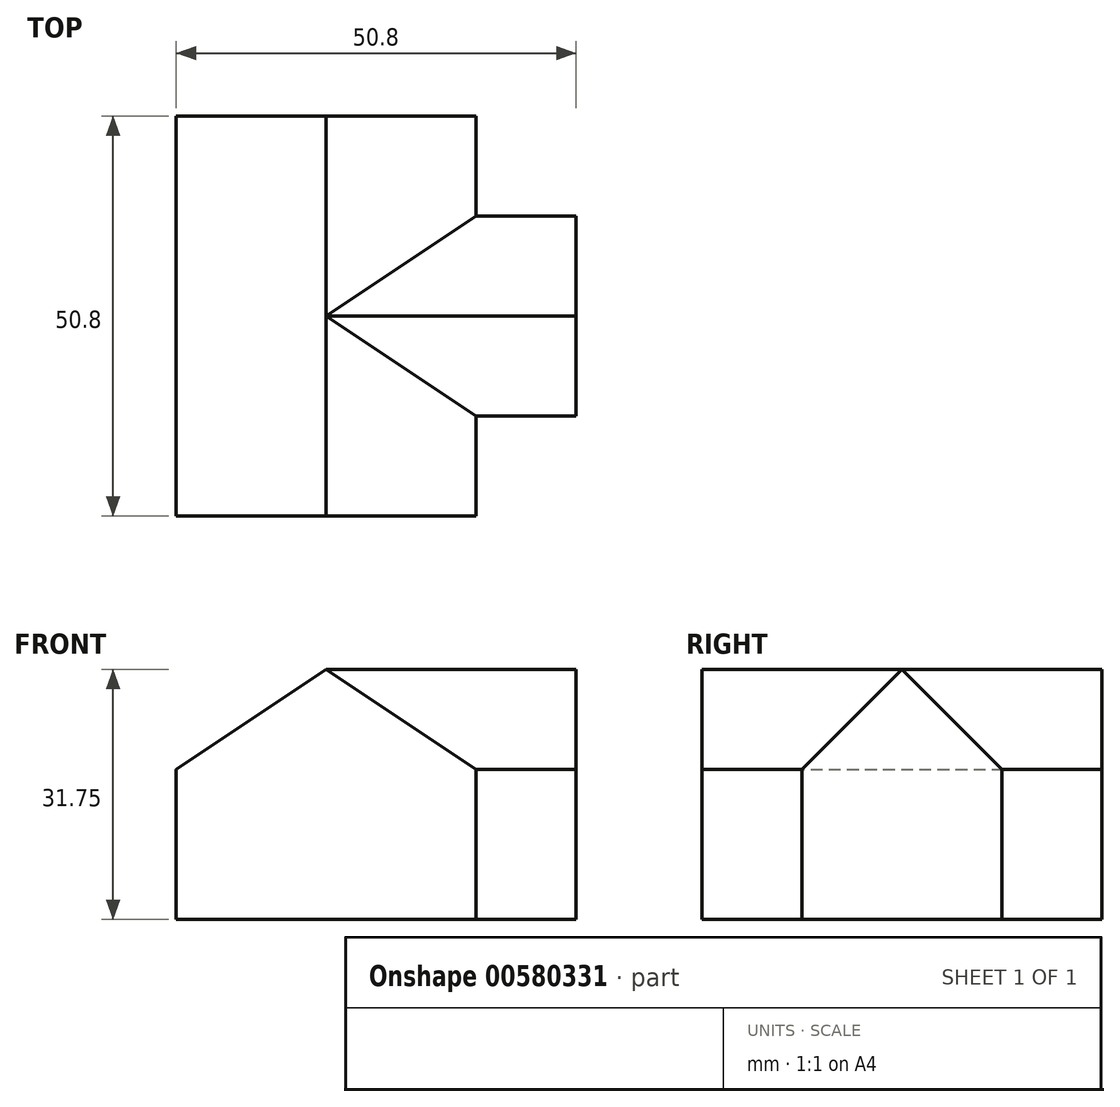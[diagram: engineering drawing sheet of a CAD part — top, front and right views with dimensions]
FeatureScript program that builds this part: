
annotation { "Feature Type Name" : "Feature", "Feature Type Description" : "" }
export const myFeature = defineFeature(function(context is Context, id is Id, definition is map)
    precondition{}
    {
        {
            var Q0;
            Q0=qCreatedBy(makeId("Front.planeOp"),FACE);
            var sketch = newSketch(context, id + "F0", { "sketchPlane" : qUnion([Q0])});
            skLineSegment(sketch, "E0", {"start": v(0, 0) * mm, "end": v(0, 19.05) * mm});
            skLineSegment(sketch, "E1", {"start": v(0, 19.05) * mm, "end": v(0, 0) * mm});
            skLineSegment(sketch, "E2", {"start": v(38.1, 0) * mm, "end": v(0, 0) * mm});
            skLineSegment(sketch, "E3", {"start": v(38.1, 0) * mm, "end": v(38.1, 19.05) * mm});
            skLineSegment(sketch, "E4", {"start": v(0, 19.05) * mm, "end": v(19.05, 31.75) * mm});
            skLineSegment(sketch, "E5", {"start": v(38.1, 19.05) * mm, "end": v(38.1, 31.75) * mm});
            skLineSegment(sketch, "E6", {"start": v(38.1, 31.75) * mm, "end": v(19.05, 31.75) * mm});
            skSolve(sketch);
        }
        {
            var Q0;
            Q0=makeQuery(id+"F0.imprint","IMPRINT",FACE,{"disambiguationData":[TD([[makeQuery(id+"F0.imprint","IMPRINT",EDGE,{"derivedFrom":sQuery(id+"F0.wireOp",EDGE,"E1")}),1.0]])]});
            var Q1;
            Q1=makeQuery(id+"F0.imprint","IMPRINT",FACE,{"disambiguationData":[TD([[makeQuery(id+"F0.imprint","IMPRINT",EDGE,{"derivedFrom":sQuery(id+"F0.wireOp",EDGE,"E4")}),-1.0]])]});
            extrude(context, id + "F1", {"entities" : qUnion([Q0, Q1]), "depth" : 50.8 * mm, "offsetDistance" : 25.4 * mm});
        }
        {
            var Q0;
            Q0=makeQuery(id+"F1.opExtrude","SWEPT_FACE",FACE,{"disambiguationData":[OSD([sQuery(id+"F0.wireOp",EDGE,"E3"),sQuery(id+"F0.wireOp",EDGE,"E5")])]});
            var sketch = newSketch(context, id + "F2", { "sketchPlane" : qUnion([Q0])});
            skLineSegment(sketch, "E7", {"start": v(-50.8, 31.75) * mm, "end": v(-38.1, 31.75) * mm});
            skLineSegment(sketch, "E8", {"start": v(-38.1, 31.75) * mm, "end": v(-38.1, 0) * mm});
            skLineSegment(sketch, "E9", {"start": v(-12.7, 0) * mm, "end": v(-38.1, 0) * mm});
            skLineSegment(sketch, "E10", {"start": v(-12.7, 0) * mm, "end": v(-12.7, 31.75) * mm});
            skSolve(sketch);
        }
        {
            var Q0;
            {var subQ0=sQuery(id+"F2.wireOp",EDGE,"E8");Q0=makeQuery(id+"F2.imprint","IMPRINT",FACE,{"disambiguationData":[TD([[makeQuery(id+"F2.imprint","IMPRINT",EDGE,{"derivedFrom":subQ0}),1.0]])]});}
            extrude(context, id + "F3", {"entities" : qUnion([Q0]), "operationType" : NewBodyOperationType.ADD, "depth" : 12.7 * mm, "offsetDistance" : 25.4 * mm});
        }
        {
            var Q0;
            Q0=makeQuery(id+"F1.opExtrude","CAP_FACE",FACE,{"disambiguationData":[OSD([sQuery(id+"F0.wireOp",EDGE,"E1"),sQuery(id+"F0.wireOp",EDGE,"E2"),sQuery(id+"F0.wireOp",EDGE,"E3"),sQuery(id+"F0.wireOp",EDGE,"E4"),sQuery(id+"F0.wireOp",EDGE,"E5"),sQuery(id+"F0.wireOp",EDGE,"E6")])],"isStart":false});
            var sketch = newSketch(context, id + "F4", { "sketchPlane" : qUnion([Q0])});
            skLineSegment(sketch, "E11", {"start": v(19.05, 31.75) * mm, "end": v(38.1, 19.05) * mm});
            skSolve(sketch);
        }
        {
            var Q0;
            {var subQ0=sQuery(id+"F4.wireOp",EDGE,"E11");Q0=makeQuery(id+"F4.imprint","IMPRINT",FACE,{"disambiguationData":[TD([[makeQuery(id+"F4.imprint","IMPRINT",EDGE,{"derivedFrom":subQ0}),1.0]])]});}
            extrude(context, id + "F5", {"entities" : qUnion([Q0]), "operationType" : NewBodyOperationType.REMOVE, "oppositeDirection" : true, "depth" : 50.8 * mm, "offsetDistance" : 25.4 * mm});
        }
        {
            var Q0;
            Q0=makeQuery(id+"F3.opExtrude","CAP_FACE",FACE,{"disambiguationData":[OSD([sQuery(id+"F0.wireOp",EDGE,"E5"),sQuery(id+"F0.wireOp",EDGE,"E6"),sQuery(id+"F2.wireOp",EDGE,"E8"),sQuery(id+"F2.wireOp",EDGE,"E9"),sQuery(id+"F2.wireOp",EDGE,"E10")])],"isStart":false});
            var sketch = newSketch(context, id + "F6", { "sketchPlane" : qUnion([Q0])});
            skLineSegment(sketch, "E12", {"start": v(-38.1, 0) * mm, "end": v(-38.1, 19.05) * mm});
            skLineSegment(sketch, "E13", {"start": v(-38.1, 19.05) * mm, "end": v(-25.4, 31.75) * mm});
            skLineSegment(sketch, "E14", {"start": v(-25.4, 31.75) * mm, "end": v(-12.7, 19.05) * mm});
            skSolve(sketch);
        }
        {
            var Q0;
            {var subQ0=sQuery(id+"F6.wireOp",EDGE,"E13");Q0=makeQuery(id+"F6.imprint","IMPRINT",FACE,{"disambiguationData":[TD([[makeQuery(id+"F6.imprint","IMPRINT",EDGE,{"derivedFrom":subQ0}),1.0]])]});}
            var Q1;
            {var subQ0=sQuery(id+"F6.wireOp",EDGE,"E14");Q1=makeQuery(id+"F6.imprint","IMPRINT",FACE,{"disambiguationData":[TD([[makeQuery(id+"F6.imprint","IMPRINT",EDGE,{"derivedFrom":subQ0}),1.0]])]});}
            extrude(context, id + "F7", {"entities" : qUnion([Q0, Q1]), "operationType" : NewBodyOperationType.REMOVE, "oppositeDirection" : true, "depth" : 12.7 * mm, "offsetDistance" : 25.4 * mm});
        }
        {
            var Q0;
            Q0=makeQuery(id+"F3.opExtrude","CAP_FACE",FACE,{"disambiguationData":[OSD([sQuery(id+"F0.wireOp",EDGE,"E5"),sQuery(id+"F0.wireOp",EDGE,"E6"),sQuery(id+"F2.wireOp",EDGE,"E8"),sQuery(id+"F2.wireOp",EDGE,"E9"),sQuery(id+"F2.wireOp",EDGE,"E10")])],"isStart":false});
            extrude(context, id + "F8", {"entities" : qUnion([Q0]), "operationType" : NewBodyOperationType.ADD, "oppositeDirection" : true, "depth" : 31.75 * mm, "offsetDistance" : 25.4 * mm});
        }
    });
